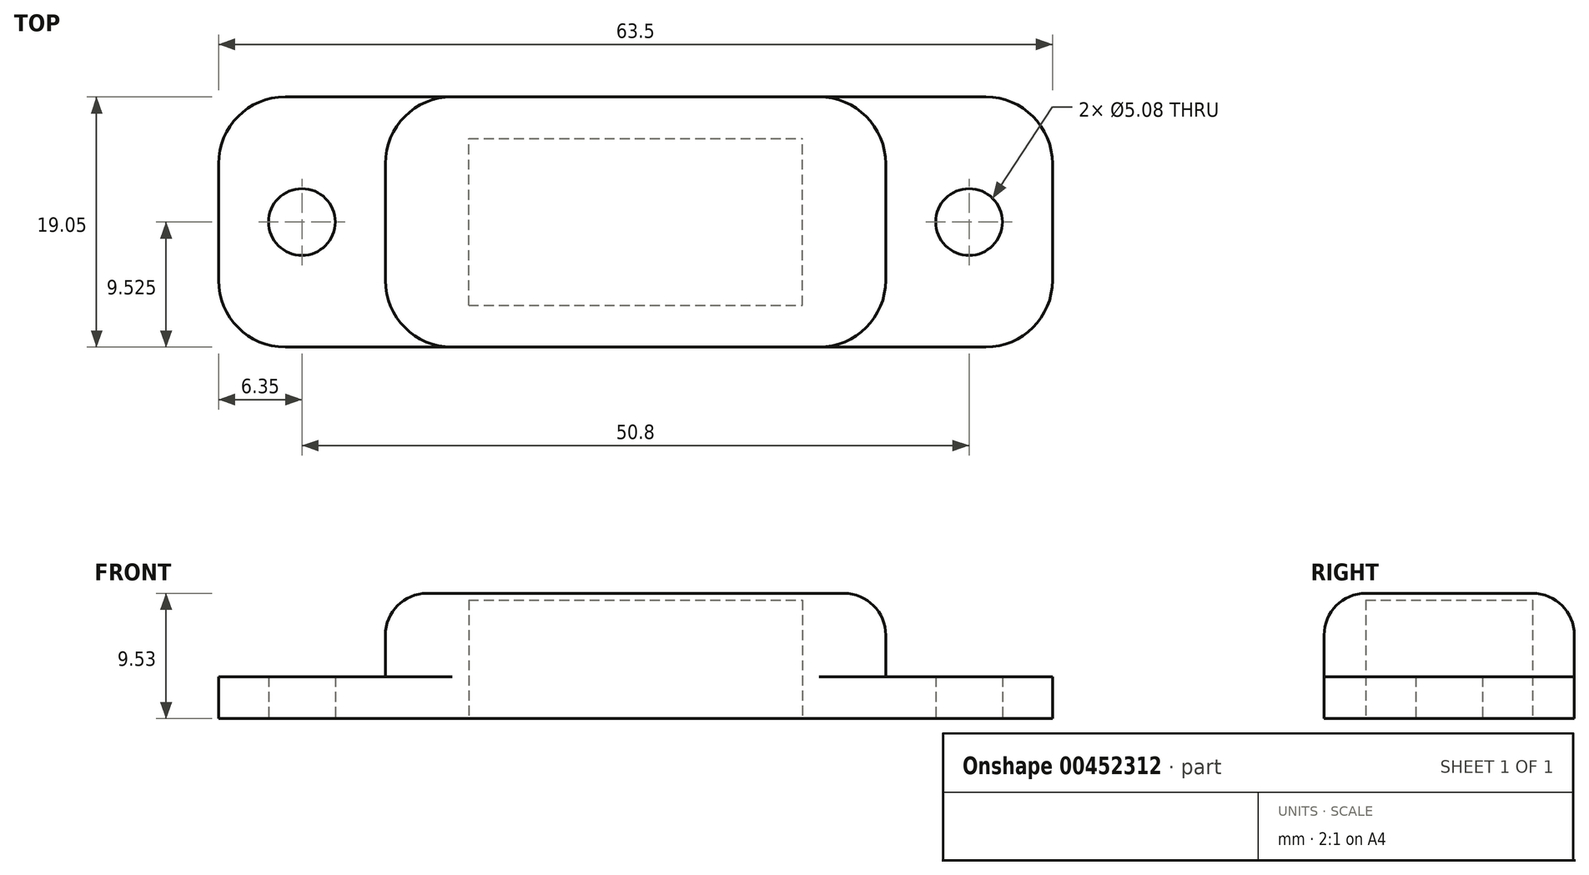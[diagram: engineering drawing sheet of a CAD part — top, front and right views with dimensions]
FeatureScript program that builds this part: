
annotation { "Feature Type Name" : "Feature", "Feature Type Description" : "" }
export const myFeature = defineFeature(function(context is Context, id is Id, definition is map)
    precondition{}
    {
        {
            var Q0;
            Q0=qCreatedBy(makeId("Front.planeOp"),FACE);
            var sketch = newSketch(context, id + "F0", { "sketchPlane" : qUnion([Q0])});
            skLineSegment(sketch, "E0.bottom", {"start": v(0, 0) * mm, "end": v(12.7, 0) * mm});
            skLineSegment(sketch, "E1", {"start": v(31.75, 3.18) * mm, "end": v(31.75, 0) * mm});
            skLineSegment(sketch, "E2", {"start": v(31.75, 0) * mm, "end": v(12.7, 0) * mm});
            skPoint(sketch, "E0.left.end.orphan", {"position": v(-19.05, 9.52) * mm});
            skPoint(sketch, "E0.left.start.orphan", {"position": v(-12.7, 0) * mm});
            skLineSegment(sketch, "E3.MirrorCS", {"start": v(-31.75, 3.18) * mm, "end": v(-31.75, 0) * mm});
            skLineSegment(sketch, "E4.MirrorCS", {"start": v(-31.75, 0) * mm, "end": v(-12.7, 0) * mm});
            skLineSegment(sketch, "E5.MirrorCS", {"start": v(0, 0) * mm, "end": v(-12.7, 0) * mm});
            skLineSegment(sketch, "E6", {"start": v(31.75, 3.18) * mm, "end": v(19.05, 3.17) * mm});
            skLineSegment(sketch, "E7", {"start": v(19.05, 3.18) * mm, "end": v(19.05, 9.53) * mm});
            skLineSegment(sketch, "E8", {"start": v(-19.05, 9.52) * mm, "end": v(-19.05, 3.18) * mm});
            skLineSegment(sketch, "E9", {"start": v(-19.05, 3.17) * mm, "end": v(-31.75, 3.17) * mm});
            skLineSegment(sketch, "E10", {"start": v(-19.05, 9.52) * mm, "end": v(19.05, 9.53) * mm});
            skSolve(sketch);
        }
        {
            var Q0;
            Q0=makeQuery(id+"F0.imprint","IMPRINT",FACE,{"disambiguationData":[TD([[makeQuery(id+"F0.imprint","IMPRINT",EDGE,{"derivedFrom":sQuery(id+"F0.wireOp",EDGE,"E0.bottom")}),1.0]])]});
            extrude(context, id + "F1", {"entities" : qUnion([Q0]), "depth" : 19.05 * mm});
        }
        {
            var Q0;
            Q0=makeQuery(id+"F1.opExtrude","SWEPT_FACE",FACE,{"disambiguationData":[OSD([sQuery(id+"F0.wireOp",EDGE,"E0.bottom"),sQuery(id+"F0.wireOp",EDGE,"E2"),sQuery(id+"F0.wireOp",EDGE,"E4.MirrorCS"),sQuery(id+"F0.wireOp",EDGE,"E5.MirrorCS")])]});
            var sketch = newSketch(context, id + "F2", { "sketchPlane" : qUnion([Q0])});
            skCircle(sketch, "E11", {"center": v(-25.4, 9.52) * mm, "radius": 2.54 * mm});
            skLineSegment(sketch, "E12", {"start": v(31.75, 9.53) * mm, "end": v(23.29, 9.53) * mm});
            skCircle(sketch, "E13.MirrorC", {"center": v(-25.4, 9.53) * mm, "radius": 2.54 * mm});
            skCircle(sketch, "E14.MirrorC", {"center": v(25.4, 9.53) * mm, "radius": 2.54 * mm});
            skSolve(sketch);
        }
        {
            var Q0;
            Q0=qSketchRegion(id+"F2",true);
            extrude(context, id + "F3", {"entities" : qUnion([Q0]), "operationType" : NewBodyOperationType.REMOVE, "oppositeDirection" : true, "depth" : 25.4 * mm});
        }
        {
            var Q0;
            Q0=makeQuery(id+"F1.opExtrude","CAP_EDGE",EDGE,{"disambiguationData":[OSD([sQuery(id+"F0.wireOp",EDGE,"E3.MirrorCS")])],"isStart":false});
            var Q1;
            Q1=makeQuery(id+"F1.opExtrude","CAP_EDGE",EDGE,{"disambiguationData":[OSD([sQuery(id+"F0.wireOp",EDGE,"E1")])],"isStart":false});
            var Q2;
            Q2=makeQuery(id+"F1.opExtrude","CAP_EDGE",EDGE,{"disambiguationData":[OSD([sQuery(id+"F0.wireOp",EDGE,"E1")])],"isStart":true});
            var Q3;
            Q3=makeQuery(id+"F1.opExtrude","CAP_EDGE",EDGE,{"disambiguationData":[OSD([sQuery(id+"F0.wireOp",EDGE,"E3.MirrorCS")])],"isStart":true});
            var Q4;
            Q4=makeQuery(id+"F1.opExtrude","CAP_EDGE",EDGE,{"disambiguationData":[OSD([sQuery(id+"F0.wireOp",EDGE,"E7")])],"isStart":true});
            var Q5;
            Q5=makeQuery(id+"F1.opExtrude","CAP_EDGE",EDGE,{"disambiguationData":[OSD([sQuery(id+"F0.wireOp",EDGE,"E8")])],"isStart":true});
            var Q6;
            Q6=makeQuery(id+"F1.opExtrude","CAP_EDGE",EDGE,{"disambiguationData":[OSD([sQuery(id+"F0.wireOp",EDGE,"E7")])],"isStart":false});
            var Q7;
            Q7=makeQuery(id+"F1.opExtrude","CAP_EDGE",EDGE,{"disambiguationData":[OSD([sQuery(id+"F0.wireOp",EDGE,"E8")])],"isStart":false});
            fillet(context, id + "F4", {"entities" : qUnion([Q0, Q1, Q2, Q3, Q4, Q5, Q6, Q7]), "radius" : 5.08 * mm, "tangentPropagation" : true, "allowEdgeOverflow" : false});
        }
        {
            var Q0;
            Q0=makeQuery(id+"F4.opFillet","BLEND_EDGE",EDGE,{"blendedFrom":[makeQuery(id+"F1.opExtrude","CAP_EDGE",EDGE,{"disambiguationData":[OSD([sQuery(id+"F0.wireOp",EDGE,"E8")])],"isStart":false}),makeQuery(id+"F1.opExtrude","SWEPT_FACE",FACE,{"disambiguationData":[OSD([sQuery(id+"F0.wireOp",EDGE,"E10")])]})],"blendedInto":[makeQuery(id+"F1.opExtrude","SWEPT_FACE",FACE,{"disambiguationData":[OSD([sQuery(id+"F0.wireOp",EDGE,"E10")])]})]});
            fillet(context, id + "F5", {"entities" : qUnion([Q0]), "radius" : 3.17 * mm, "tangentPropagation" : true, "allowEdgeOverflow" : false});
        }
        {
            var Q0;
            Q0=makeQuery(id+"F1.opExtrude","SWEPT_FACE",FACE,{"disambiguationData":[OSD([sQuery(id+"F0.wireOp",EDGE,"E0.bottom"),sQuery(id+"F0.wireOp",EDGE,"E2"),sQuery(id+"F0.wireOp",EDGE,"E4.MirrorCS"),sQuery(id+"F0.wireOp",EDGE,"E5.MirrorCS")])]});
            var sketch = newSketch(context, id + "F6", { "sketchPlane" : qUnion([Q0])});
            skLineSegment(sketch, "E15.bottom", {"start": v(-12.7, 15.87) * mm, "end": v(12.7, 15.88) * mm});
            skLineSegment(sketch, "E15.top", {"start": v(-12.7, 3.17) * mm, "end": v(12.7, 3.18) * mm});
            skLineSegment(sketch, "E15.left", {"start": v(-12.7, 15.87) * mm, "end": v(-12.7, 3.17) * mm});
            skLineSegment(sketch, "E15.right", {"start": v(12.7, 15.88) * mm, "end": v(12.7, 3.18) * mm});
            skSolve(sketch);
        }
        {
            var Q0;
            Q0=qSketchRegion(id+"F6",true);
            extrude(context, id + "F7", {"entities" : qUnion([Q0]), "operationType" : NewBodyOperationType.REMOVE, "oppositeDirection" : true, "depth" : 9.02 * mm});
        }
    });
